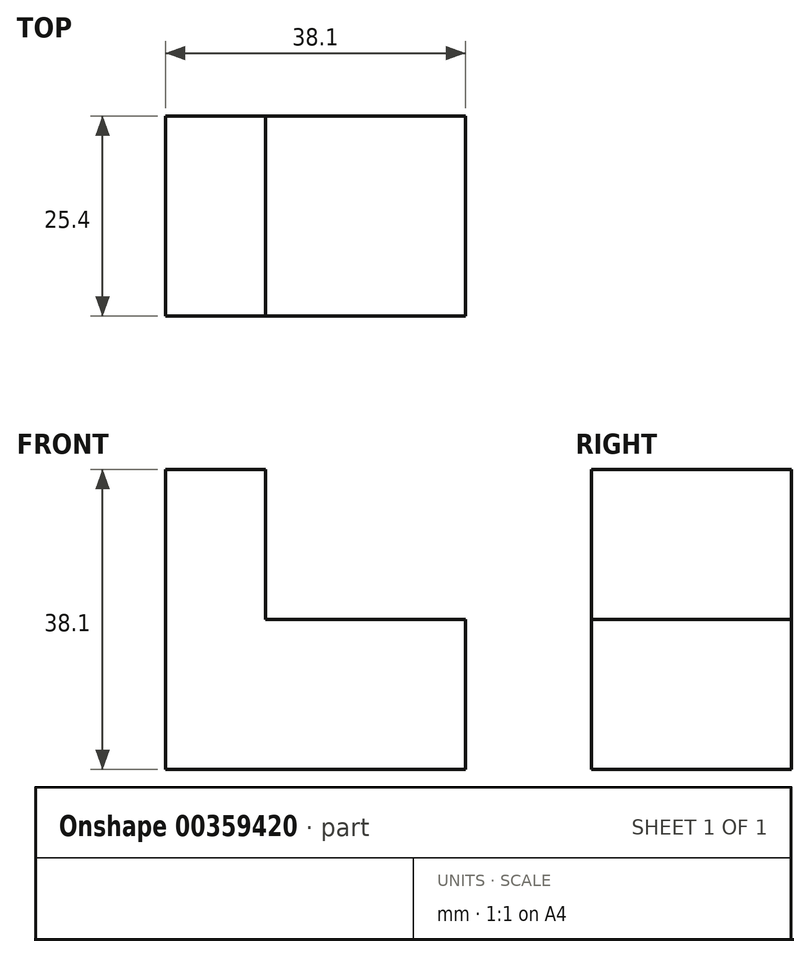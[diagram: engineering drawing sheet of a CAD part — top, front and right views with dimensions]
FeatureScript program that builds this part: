
annotation { "Feature Type Name" : "Feature", "Feature Type Description" : "" }
export const myFeature = defineFeature(function(context is Context, id is Id, definition is map)
    precondition{}
    {
        {
            var Q0;
            Q0=qCreatedBy(makeId("Front.planeOp"),FACE);
            var sketch = newSketch(context, id + "F0", { "sketchPlane" : qUnion([Q0])});
            skLineSegment(sketch, "E0", {"start": v(0, 0) * mm, "end": v(0, 38.1) * mm});
            skLineSegment(sketch, "E1", {"start": v(0, 38.1) * mm, "end": v(12.7, 38.1) * mm});
            skLineSegment(sketch, "E2", {"start": v(12.7, 38.1) * mm, "end": v(12.7, 19.05) * mm});
            skLineSegment(sketch, "E3", {"start": v(12.7, 19.05) * mm, "end": v(38.1, 19.05) * mm});
            skLineSegment(sketch, "E4", {"start": v(38.1, 19.05) * mm, "end": v(38.1, 0) * mm});
            skLineSegment(sketch, "E5", {"start": v(38.1, 0) * mm, "end": v(0, 0) * mm});
            skSolve(sketch);
        }
        {
            var Q0;
            Q0 = qSketchRegion(id + "F0", true);
            extrude(context, id + "F1", {"entities" : qUnion([Q0]), "depth" : 25.4 * mm});
        }
    });
